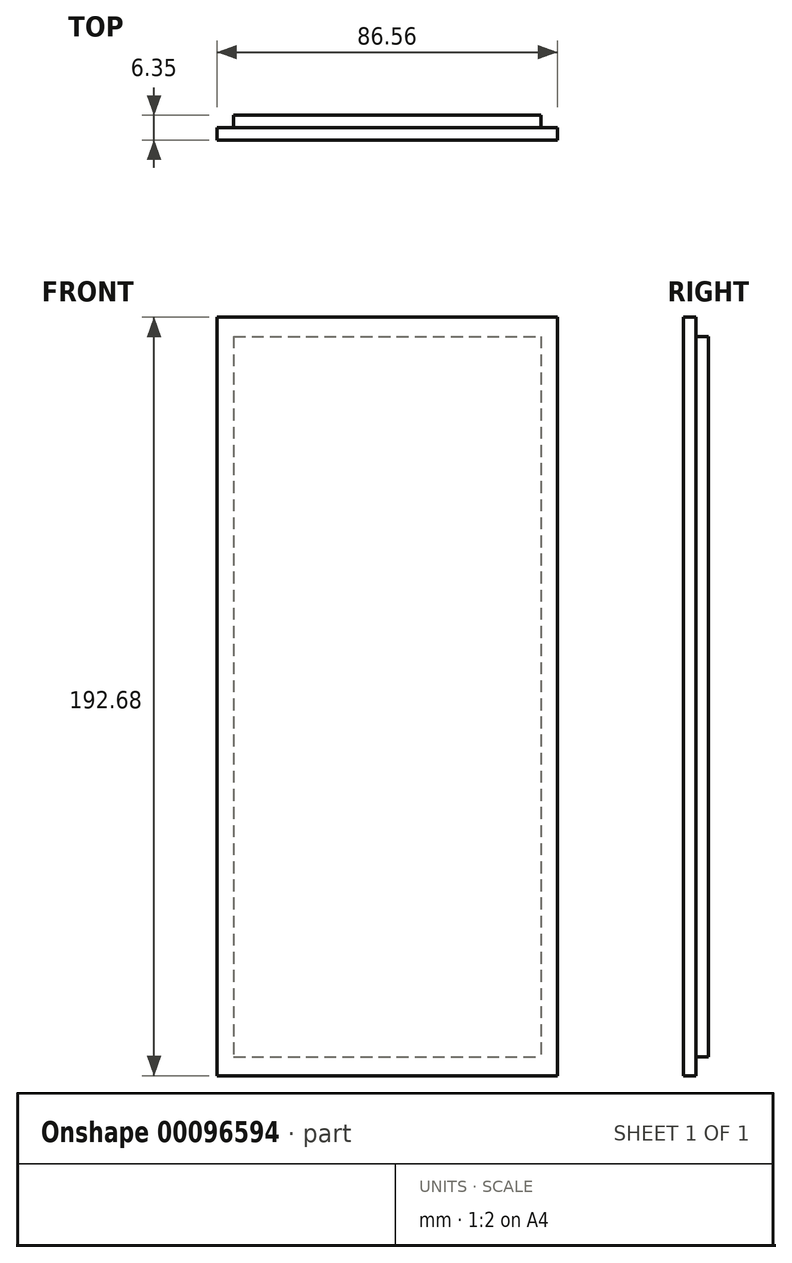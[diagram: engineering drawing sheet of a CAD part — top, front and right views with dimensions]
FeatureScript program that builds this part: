
annotation { "Feature Type Name" : "Feature", "Feature Type Description" : "" }
export const myFeature = defineFeature(function(context is Context, id is Id, definition is map)
    precondition{}
    {
        {
            var Q0;
            Q0=qCreatedBy(makeId("Front.planeOp"),FACE);
            var sketch = newSketch(context, id + "F0", { "sketchPlane" : qUnion([Q0])});
            skLineSegment(sketch, "E0.bottom", {"start": v(-39, 91.5) * mm, "end": v(39, 91.5) * mm});
            skLineSegment(sketch, "E0.top", {"start": v(-39, -91.5) * mm, "end": v(39, -91.5) * mm});
            skLineSegment(sketch, "E0.left", {"start": v(-39, 91.5) * mm, "end": v(-39, -91.5) * mm});
            skLineSegment(sketch, "E0.right", {"start": v(39, 91.5) * mm, "end": v(39, -91.5) * mm});
            skPoint(sketch, "E0.middle", {"position": v(0, 0) * mm});
            skSolve(sketch);
        }
        {
            var Q0;
            Q0 = qSketchRegion(id + "F0", true);
            extrude(context, id + "F1", {"entities" : qUnion([Q0]), "depth" : 3.17 * mm});
        }
        {
            var Q0;
            Q0=makeQuery(id+"F1.opExtrude","CAP_FACE",FACE,{"disambiguationData":[OSD([sQuery(id+"F0.wireOp",EDGE,"E0.bottom"),sQuery(id+"F0.wireOp",EDGE,"E0.top"),sQuery(id+"F0.wireOp",EDGE,"E0.left"),sQuery(id+"F0.wireOp",EDGE,"E0.right")])],"isStart":false});
            var sketch = newSketch(context, id + "F2", { "sketchPlane" : qUnion([Q0])});
            skLineSegment(sketch, "E1.bottom", {"start": v(43.28, 96.34) * mm, "end": v(-43.28, 96.34) * mm});
            skLineSegment(sketch, "E1.top", {"start": v(43.28, -96.34) * mm, "end": v(-43.28, -96.34) * mm});
            skLineSegment(sketch, "E1.left", {"start": v(43.28, 96.34) * mm, "end": v(43.28, -96.34) * mm});
            skLineSegment(sketch, "E1.right", {"start": v(-43.28, 96.34) * mm, "end": v(-43.28, -96.34) * mm});
            skPoint(sketch, "E1.middle", {"position": v(0, 0) * mm});
            skSolve(sketch);
        }
        {
            var Q0;
            Q0 = qSketchRegion(id + "F2", true);
            extrude(context, id + "F3", {"entities" : qUnion([Q0]), "operationType" : NewBodyOperationType.ADD, "depth" : 3.17 * mm});
        }
    });
